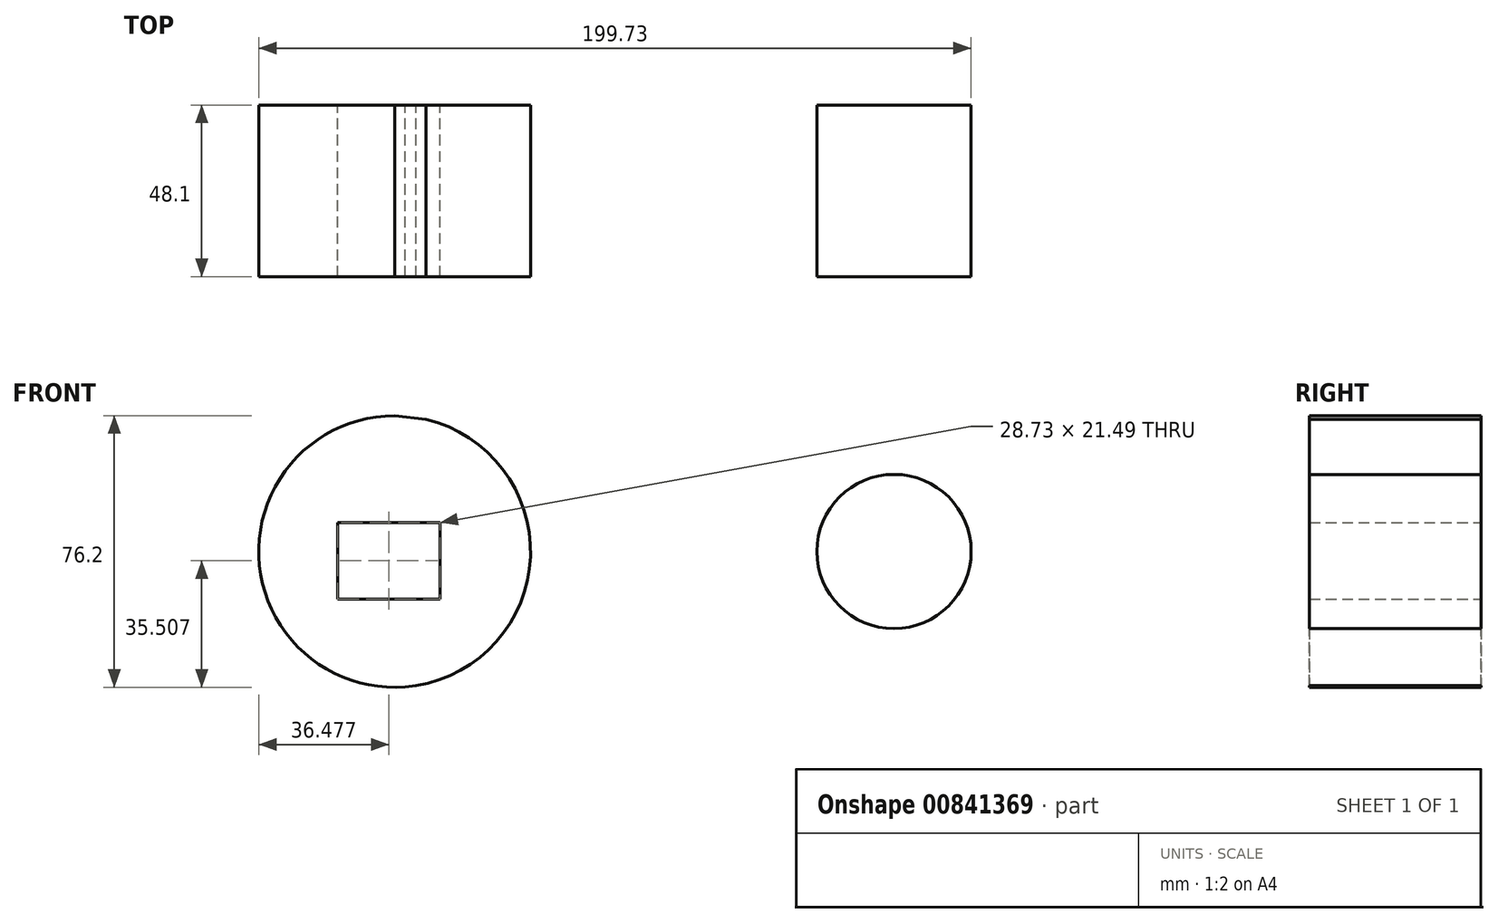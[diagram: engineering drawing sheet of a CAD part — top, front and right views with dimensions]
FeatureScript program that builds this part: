
annotation { "Feature Type Name" : "Feature", "Feature Type Description" : "" }
export const myFeature = defineFeature(function(context is Context, id is Id, definition is map)
    precondition{}
    {
        {
            var Q0;
            Q0=qCreatedBy(makeId("Front.planeOp"),FACE);
            var sketch = newSketch(context, id + "F0", { "sketchPlane" : qUnion([Q0])});
            skCircle(sketch, "E0", {"center": v(0, 0) * mm, "radius": 38.1 * mm});
            skCircle(sketch, "E1", {"center": v(140, 0) * mm, "radius": 21.63 * mm});
            skLineSegment(sketch, "E2", {"start": v(0, 38.1) * mm, "end": v(142.5, 21.48) * mm});
            skLineSegment(sketch, "E3", {"start": v(2.96, -37.99) * mm, "end": v(142.5, -21.48) * mm});
            skLineSegment(sketch, "E4.bottom", {"start": v(-15.99, -13.34) * mm, "end": v(12.74, -13.34) * mm});
            skLineSegment(sketch, "E4.top", {"start": v(-15.99, 8.15) * mm, "end": v(12.74, 8.15) * mm});
            skLineSegment(sketch, "E4.left", {"start": v(-15.99, -13.34) * mm, "end": v(-15.99, 8.15) * mm});
            skLineSegment(sketch, "E4.right", {"start": v(12.74, -13.34) * mm, "end": v(12.74, 8.15) * mm});
            skLineSegment(sketch, "E5.top", {"start": v(-9.56, 5.21) * mm, "end": v(5.03, 5.21) * mm});
            skLineSegment(sketch, "E5.left", {"start": v(-9.56, -5.43) * mm, "end": v(-9.56, 5.21) * mm});
            skSolve(sketch);
        }
        {
            var Q0;
            {var subQ0=sQuery(id+"F0.wireOp",EDGE,"E2");var subQ1=sQuery(id+"F0.wireOp",EDGE,"E0");var subQ2=makeQuery(id+"F0.imprint","INTERSECT",VERTEX,{"disambiguationData":[OD(0.0)],"derivedFrom":[subQ1,subQ0]});Q0=makeQuery(id+"F0.imprint","IMPRINT",FACE,{"disambiguationData":[TD([[makeQuery(id+"F0.imprint","IMPRINT",EDGE,{"disambiguationData":[TD([[subQ2,1.0]])],"derivedFrom":subQ1}),1.0]])]});}
            var Q1;
            {var subQ0=sQuery(id+"F0.wireOp",EDGE,"E3");var subQ1=sQuery(id+"F0.wireOp",EDGE,"E0");var subQ2=makeQuery(id+"F0.imprint","INTERSECT",VERTEX,{"disambiguationData":[OD(0.0)],"derivedFrom":[subQ1,subQ0]});Q1=makeQuery(id+"F0.imprint","IMPRINT",FACE,{"disambiguationData":[TD([[makeQuery(id+"F0.imprint","IMPRINT",EDGE,{"disambiguationData":[TD([[subQ2,-1.0]])],"derivedFrom":subQ1}),1.0]])]});}
            var Q2;
            {var subQ0=sQuery(id+"F0.wireOp",EDGE,"E1");var subQ1=makeQuery(id+"F0.imprint","INTERSECT",VERTEX,{"derivedFrom":[subQ0,sQuery(id+"F0.wireOp",EDGE,"E2")]});Q2=makeQuery(id+"F0.imprint","IMPRINT",FACE,{"disambiguationData":[TD([[makeQuery(id+"F0.imprint","IMPRINT",EDGE,{"disambiguationData":[TD([[subQ1,-1.0]])],"derivedFrom":subQ0}),1.0]])]});}
            var Q3;
            {var subQ0=sQuery(id+"F0.wireOp",EDGE,"E2");var subQ1=sQuery(id+"F0.wireOp",EDGE,"E0");var subQ2=makeQuery(id+"F0.imprint","INTERSECT",VERTEX,{"disambiguationData":[OD(1.0)],"derivedFrom":[subQ1,subQ0]});Q3=makeQuery(id+"F0.imprint","IMPRINT",FACE,{"disambiguationData":[TD([[makeQuery(id+"F0.imprint","IMPRINT",EDGE,{"disambiguationData":[TD([[subQ2,1.0]])],"derivedFrom":subQ1}),-1.0]])]});}
            var Q4;
            Q4=makeQuery(id+"F0.imprint","IMPRINT",FACE,{"disambiguationData":[TD([[makeQuery(id+"F0.imprint","IMPRINT",EDGE,{"derivedFrom":sQuery(id+"F0.wireOp",EDGE,"E4.bottom")}),-1.0]])]});
            extrude(context, id + "F1", {"entities" : qUnion([Q0, Q1, Q2, Q3, Q4]), "depth" : 48.1 * mm, "offsetDistance" : 25 * mm});
        }
    });
